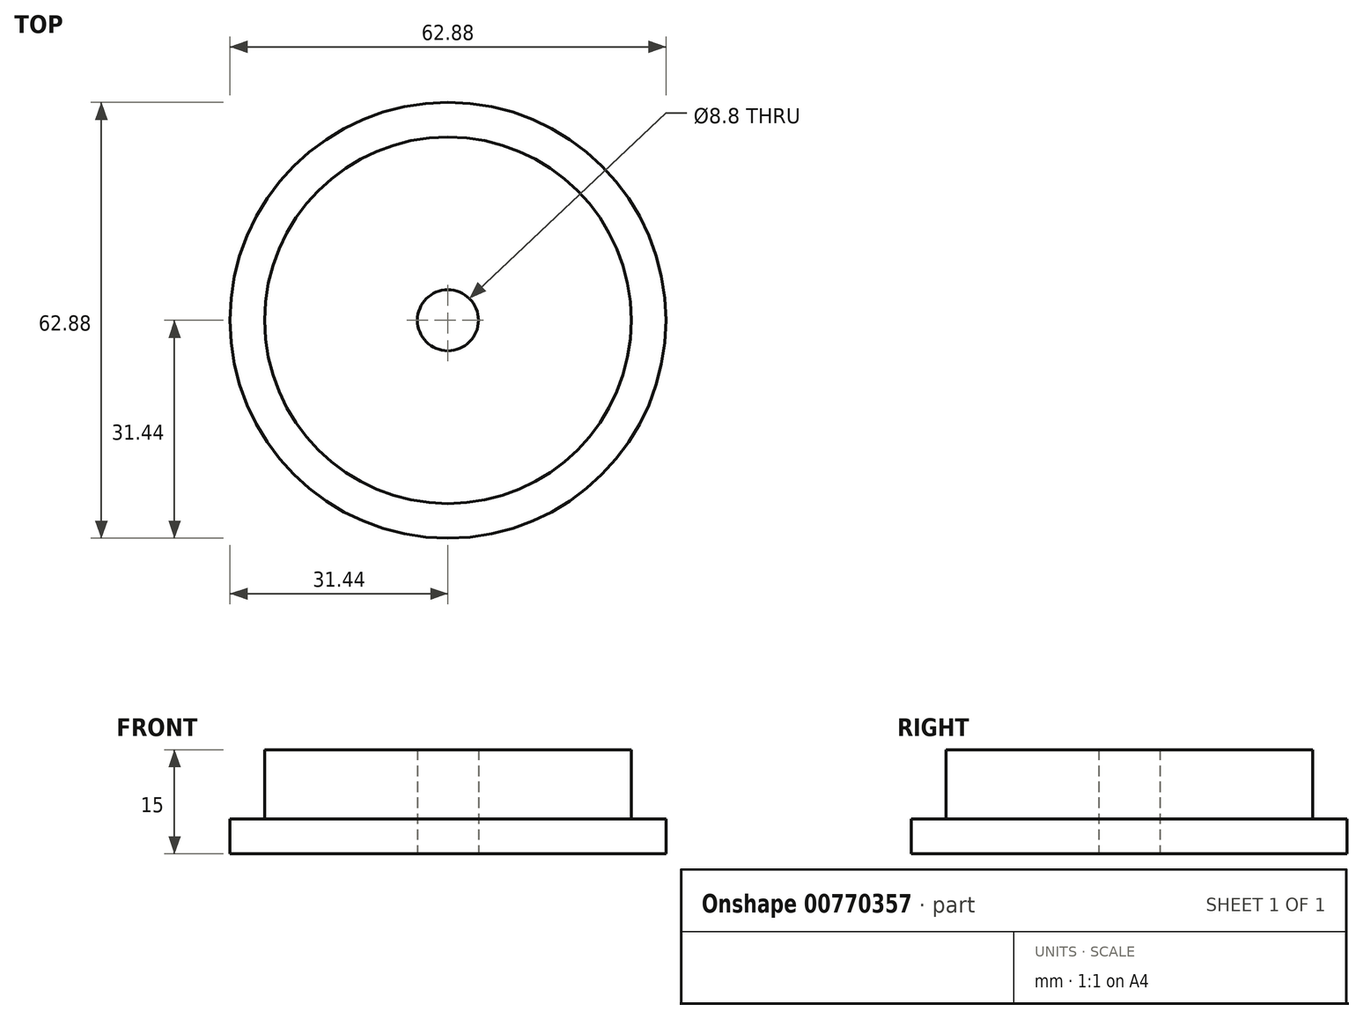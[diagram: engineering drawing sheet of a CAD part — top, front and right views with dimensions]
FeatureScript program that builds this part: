
annotation { "Feature Type Name" : "Feature", "Feature Type Description" : "" }
export const myFeature = defineFeature(function(context is Context, id is Id, definition is map)
    precondition{}
    {
        {
            var Q0;
            Q0=qCreatedBy(makeId("Front.planeOp"),FACE);
            var sketch = newSketch(context, id + "F0", { "sketchPlane" : qUnion([Q0])});
            skLineSegment(sketch, "E0", {"start": v(0, 0) * mm, "end": v(-31.44, 0) * mm});
            skLineSegment(sketch, "E1", {"start": v(-31.44, 0) * mm, "end": v(-31.44, 5) * mm});
            skLineSegment(sketch, "E2", {"start": v(-31.44, 5) * mm, "end": v(-26.44, 5) * mm});
            skLineSegment(sketch, "E3", {"start": v(-26.44, 5) * mm, "end": v(-26.44, 15) * mm});
            skLineSegment(sketch, "E4", {"start": v(-26.44, 15) * mm, "end": v(0, 15) * mm});
            skLineSegment(sketch, "E5", {"start": v(0, 15) * mm, "end": v(0, 0) * mm});
            skSolve(sketch);
        }
        {
            var Q0;
            Q0=makeQuery(id+"F0.imprint","IMPRINT",FACE,{"disambiguationData":[TD([[makeQuery(id+"F0.imprint","IMPRINT",EDGE,{"derivedFrom":sQuery(id+"F0.wireOp",EDGE,"E0")}),-1.0]])]});
            var Q1;
            Q1=sQuery(id+"F0.wireOp",EDGE,"E5");
            revolve(context, id + "F1", {"surfaceOperationType" : NewSurfaceOperationType.NEW, "entities" : qUnion([Q0]), "axis" : qUnion([Q1]), "revolveType" : RevolveType.FULL});
        }
        {
            var Q0;
            Q0=qCreatedBy(makeId("Top.planeOp"),FACE);
            var sketch = newSketch(context, id + "F2", { "sketchPlane" : qUnion([Q0])});
            skCircle(sketch, "E6", {"center": v(0, 0) * mm, "radius": 4.4 * mm});
            skSolve(sketch);
        }
        {
            var Q0;
            Q0=sQuery(id+"F2.wireOp",VERTEX,"E6.center");
            var Q1;
            Q1=makeQuery(id+"F1.opRevolve","SWEPT_BODY",BODY,{"disambiguationData":[OSD([sQuery(id+"F0.wireOp",EDGE,"E0"),sQuery(id+"F0.wireOp",EDGE,"E1"),sQuery(id+"F0.wireOp",EDGE,"E2"),sQuery(id+"F0.wireOp",EDGE,"E3"),sQuery(id+"F0.wireOp",EDGE,"E4"),sQuery(id+"F0.wireOp",EDGE,"E5")])]});
            hole(context, id + "F3", {"style" : HoleStyle.SIMPLE, "endStyle" : HoleEndStyle.THROUGH, "oppositeDirection" : true, "standardTappedOrClearance" : lookupTablePath({ "standard" : "ISO", "fit" : "Normal", "size" : "M8", "type" : "Clearance" }), "standardBlindInLast" : lookupTablePath({ "fit" : "Standard", "standard" : "ISO", "size" : "M8", "type" : "Clearance" }), "holeDiameter" : 8.8 * mm, "majorDiameter" : 5 * mm, "isTappedThrough" : true, "tappedDepth" : 12 * mm, "tapClearance" : 3, "locations" : qUnion([Q0]), "scope" : qUnion([Q1])});
        }
    });
